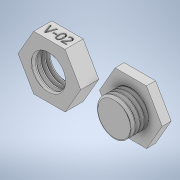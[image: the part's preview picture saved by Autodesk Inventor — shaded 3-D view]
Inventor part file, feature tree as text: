
AUTODESK INVENTOR PART (.ipt)
format: ipt  version: 2021.1 (Build 251245000, 245)  size: 563,200 bytes
history: native  units: in
note: dims shown in document units (in); Inventor stores cm internally (conversion verified against a paired STEP export)
features: sketch x9, extrude x6, helix x2
ambient origin geometry x8: Origin, YZ Plane, XZ Plane, XY Plane, X Axis, Y Axis, Z Axis, Center Point
bodies: Solid1 (feature_tree)
feature tree (17):
  extrude  "Extrusion1"  Depth=0.25in TaperAngle=0.0deg
  extrude  "Extrusion3"  TaperAngle=60.0deg  [1 undecoded]
  helix  "Coil1"  [1 undecoded]
  sketch  "Sketch5"  dims[d12=0.9755in d13=0.125in d14=0.125in]
  extrude  "Extrusion4"  Depth=0.0119in
  extrude  "Extrusion5"  Depth=0.125in
  helix  "Coil2"  [1 undecoded]
  extrude  "Extrusion6"  Depth=0.3937in
  extrude  "Extrusion7"  Depth=0.5in
  sketch  "Sketch1"  dims[d0=1.5in d1=0.25in d2=0.0in]
  sketch  "Sketch3"  dims[d6=0.5in d7=0.0in d8=60.0deg d9=0.4878in]
  sketch  "Sketch4"  dims[d10=0.0119in d11=0.4066in]
  sketch  "Sketch6"  dims[d15=0.75in]
  sketch  "Sketch7"  dims[d16=0.3937in d17=0.0in d18=90.0deg d19=90.0deg d20=0.0in d21=0.0in d22=2.0in]
  sketch  "Sketch9"  dims[d23=1.5in d24=0.5in]
  sketch  "Sketch11"  dims[d25=0.0in]
  sketch  "Sketch12"  dims[d26=0.8897in d27=0.0in d28=0.0in d29=60.0deg d30=0.4449in d31=0.0119in d32=0.5156in d33=0.125in d34=0.75in d35=0.3937in d36=0.0in d37=90.0deg d38=90.0deg d39=0.0in d40=0.0in d41=0.125in d42=0.1in d43=0.0in d44=0.1in d45=0.0in]
note: 3 required parameter values undecoded (feature->parameter linkage not recoverable at this tier; creation-order binding heuristic only, values carry confidence <= 0.55)
